# Revit family: Accessory-Container-KOHLER-Draft-K-27365
name_source: partatom
category: Specialty Equipment
revit_build: Autodesk Revit 2015 (Build: 20140606_1530(x64)
units: mm (PartAtom-declared; Revit-internal decimal feet)

## types (2) — shared parameters
ADA Compliant = No
Assembly Code = C1030200
Date Modified = 01/16/2019
Default Elevation = 42"
Description = 6 inch Container
Height = 2 1/8"
Length = 5 15/16"
Manufacturer = KOHLER Co.
MasterFormat 1995 = 10820
MasterFormat 2004 = 10.28.13
Material = Durable Composite Material
Product Documentation Link = http://www.us.kohler.com
Product Name = Draft
Product Page URL = http://www.us.kohler.com
URL = https://www.us.kohler.com
Width = 4 11/16"

## per-type parameters (varying)
| type | Finish | Model | Type |
| 0-White | Kohler-Plastic-0-White | K-27365-0 | 1 |
| 7-Black Black | Kohler-Plastic-7-Black_Black | K-27365-7 | 2 |

## geometry (parser evidence)
native form markers: Sweep x6
no freeform markers — native parametric forms only
